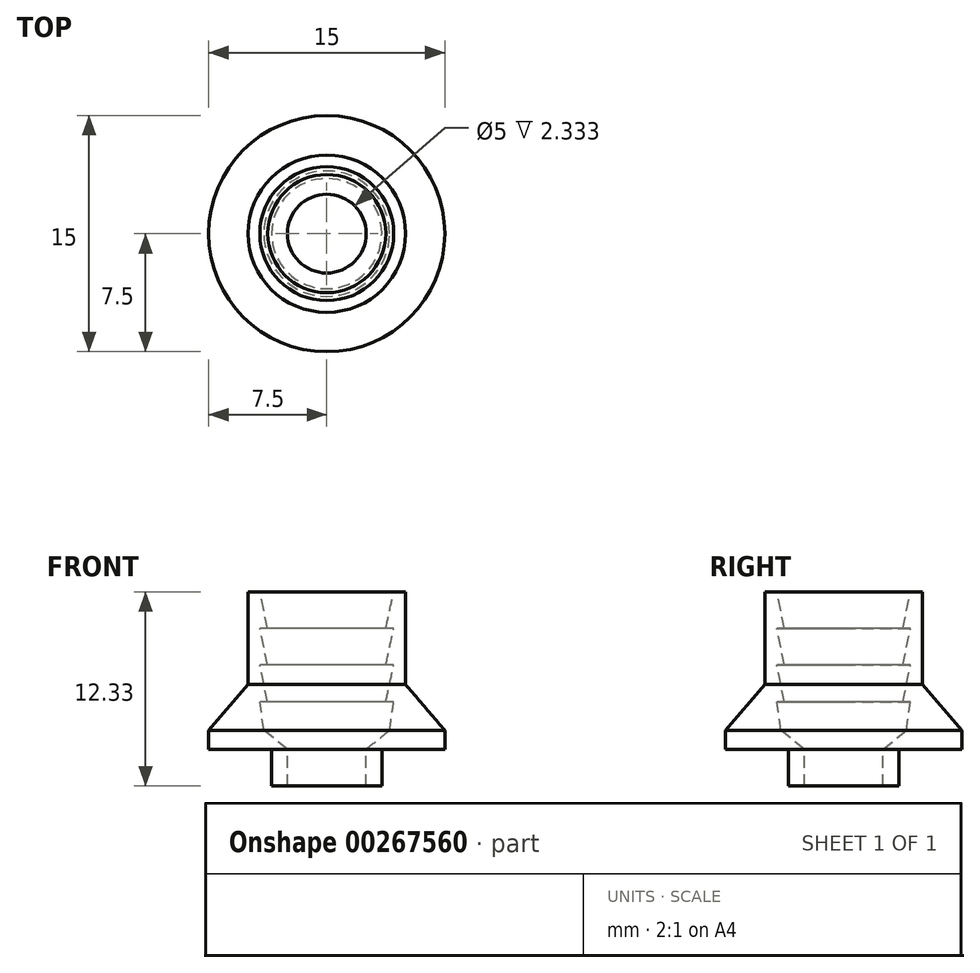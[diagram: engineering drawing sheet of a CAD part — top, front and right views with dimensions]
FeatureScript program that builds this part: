
annotation { "Feature Type Name" : "Feature", "Feature Type Description" : "" }
export const myFeature = defineFeature(function(context is Context, id is Id, definition is map)
    precondition{}
    {
        {
            var Q0;
            Q0=qCreatedBy(makeId("Top.planeOp"),FACE);
            var sketch = newSketch(context, id + "F0", { "sketchPlane" : qUnion([Q0])});
            skCircle(sketch, "E0", {"center": v(0, 0) * mm, "radius": 2.5 * mm});
            skCircle(sketch, "E1", {"center": v(0, 0) * mm, "radius": 4 * mm});
            skCircle(sketch, "E2", {"center": v(0, 0) * mm, "radius": 6 * mm});
            skCircle(sketch, "E3", {"center": v(0, 0) * mm, "radius": 7.5 * mm});
            skSolve(sketch);
        }
        {
            var Q0;
            Q0=qCreatedBy(makeId("Front.planeOp"),FACE);
            var sketch = newSketch(context, id + "F1", { "sketchPlane" : qUnion([Q0])});
            skLineSegment(sketch, "E4", {"start": v(-4.25, 10) * mm, "end": v(-3.75, 7.67) * mm});
            skLineSegment(sketch, "E5", {"start": v(-3.75, 7.67) * mm, "end": v(-4.25, 7.67) * mm});
            skLineSegment(sketch, "E6", {"start": v(-4.25, 7.67) * mm, "end": v(-3.75, 5.35) * mm});
            skLineSegment(sketch, "E7", {"start": v(-3.75, 5.35) * mm, "end": v(-4.25, 5.35) * mm});
            skLineSegment(sketch, "E8", {"start": v(-4.25, 5.35) * mm, "end": v(-3.75, 3.02) * mm});
            skLineSegment(sketch, "E9", {"start": v(-3.75, 3.02) * mm, "end": v(-4.25, 3.02) * mm});
            skLineSegment(sketch, "E10", {"start": v(-4.25, 3.02) * mm, "end": v(-3.99, 1.2) * mm});
            skLineSegment(sketch, "E11", {"start": v(0, 13.24) * mm, "end": v(0, 0) * mm});
            skLineSegment(sketch, "E12", {"start": v(0, 1.2) * mm, "end": v(0, 10) * mm});
            skLineSegment(sketch, "E13", {"start": v(-4.25, 10) * mm, "end": v(-5, 10) * mm});
            skLineSegment(sketch, "E14", {"start": v(-7.5, 1.2) * mm, "end": v(-7.5, 0) * mm});
            skLineSegment(sketch, "E15", {"start": v(-7.5, 0) * mm, "end": v(-3.5, 0) * mm});
            skLineSegment(sketch, "E16", {"start": v(-3.5, 0) * mm, "end": v(-3.5, -2.33) * mm});
            skLineSegment(sketch, "E17", {"start": v(-3.5, -2.33) * mm, "end": v(-2.5, -2.33) * mm});
            skLineSegment(sketch, "E18", {"start": v(-2.5, -2.33) * mm, "end": v(-2.5, 0) * mm});
            skLineSegment(sketch, "E19", {"start": v(-2.5, 0) * mm, "end": v(-3.99, 1.2) * mm});
            skLineSegment(sketch, "E20", {"start": v(-4, 14.04) * mm, "end": v(-4, -4.92) * mm, "construction": true});
            skLineSegment(sketch, "E21", {"start": v(-7.5, 1.2) * mm, "end": v(-5, 4.12) * mm});
            skLineSegment(sketch, "E22", {"start": v(-5, 4.12) * mm, "end": v(-5, 10) * mm});
            skSolve(sketch);
        }
        {
            var Q0;
            Q0 = qSketchRegion(id + "F1", true);
            var Q1;
            Q1=sQuery(id+"F1.wireOp",EDGE,"E11");
            revolve(context, id + "F2", {"entities" : qUnion([Q0]), "axis" : qUnion([Q1]), "revolveType" : RevolveType.FULL});
        }
    });
